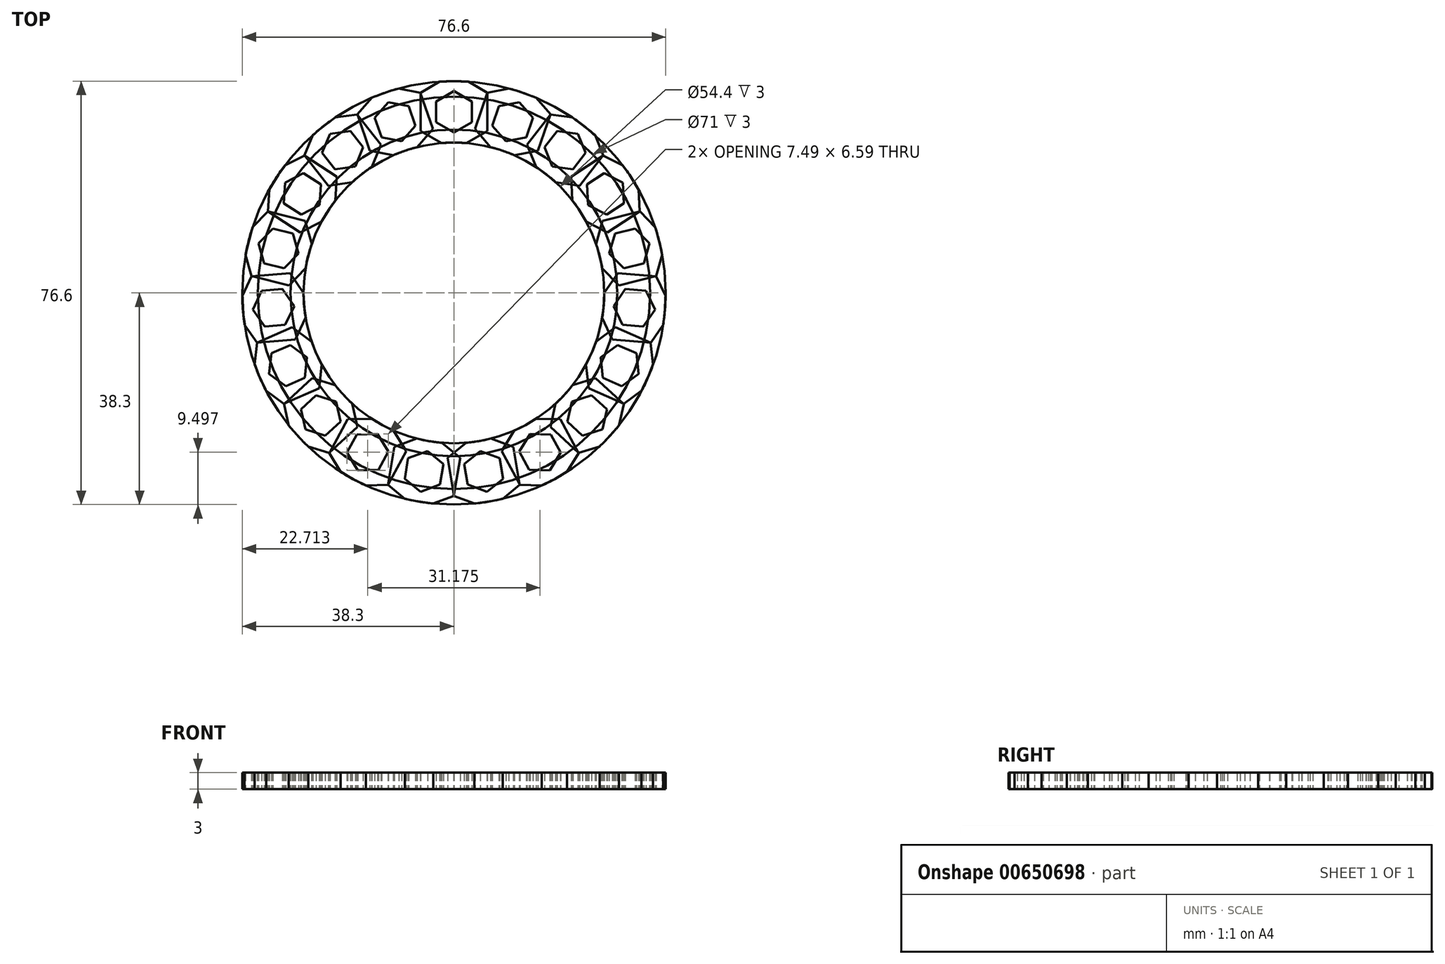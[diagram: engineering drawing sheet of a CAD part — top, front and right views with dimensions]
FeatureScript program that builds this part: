
annotation { "Feature Type Name" : "Feature", "Feature Type Description" : "" }
export const myFeature = defineFeature(function(context is Context, id is Id, definition is map)
    precondition{}
    {
        {
            var Q0;
            Q0=qCreatedBy(makeId("Top.planeOp"),FACE);
            var sketch = newSketch(context, id + "F0", { "sketchPlane" : qUnion([Q0])});
            skCircle(sketch, "E0", {"center": v(0, 0) * mm, "radius": 27.2 * mm});
            skCircle(sketch, "E1", {"center": v(0, 0) * mm, "radius": 38.3 * mm});
            skCircle(sketch, "E2", {"center": v(0, 0) * mm, "radius": 29.55 * mm});
            skCircle(sketch, "E3", {"center": v(0, 0) * mm, "radius": 35.5 * mm});
            skSolve(sketch);
        }
        {
            var Q0;
            Q0=qCreatedBy(makeId("Top.planeOp"),FACE);
            var sketch = newSketch(context, id + "F1", { "sketchPlane" : qUnion([Q0])});
            skCircle(sketch, "E4", {"center": v(0, 0) * mm, "radius": 27.2 * mm});
            skCircle(sketch, "E5", {"center": v(0, 0) * mm, "radius": 38.3 * mm});
            skLineSegment(sketch, "E6", {"start": v(0, 27.2) * mm, "end": v(0, 38.3) * mm});
            skCircle(sketch, "E7.cCircle", {"center": v(0, 32.75) * mm, "radius": 6.96 * mm, "construction": true});
            skLineSegment(sketch, "E7.0", {"start": v(0, 39.71) * mm, "end": v(6.03, 36.23) * mm});
            skLineSegment(sketch, "E7.1", {"start": v(6.03, 36.23) * mm, "end": v(6.03, 29.27) * mm});
            skLineSegment(sketch, "E7.2", {"start": v(6.03, 29.27) * mm, "end": v(0, 25.79) * mm});
            skLineSegment(sketch, "E7.3", {"start": v(0, 25.79) * mm, "end": v(-6.03, 29.27) * mm});
            skLineSegment(sketch, "E7.4", {"start": v(-6.03, 29.27) * mm, "end": v(-6.03, 36.23) * mm});
            skLineSegment(sketch, "E7.5", {"start": v(-6.03, 36.23) * mm, "end": v(0, 39.71) * mm});
            skCircle(sketch, "E8.cCircle", {"center": v(0, 32.75) * mm, "radius": 3.75 * mm, "construction": true});
            skLineSegment(sketch, "E8.0", {"start": v(0, 36.5) * mm, "end": v(3.25, 34.62) * mm});
            skLineSegment(sketch, "E8.1", {"start": v(3.25, 34.62) * mm, "end": v(3.25, 30.88) * mm});
            skLineSegment(sketch, "E8.2", {"start": v(3.25, 30.88) * mm, "end": v(0, 29) * mm});
            skLineSegment(sketch, "E8.3", {"start": v(0, 29) * mm, "end": v(-3.25, 30.88) * mm});
            skLineSegment(sketch, "E8.4", {"start": v(-3.25, 30.88) * mm, "end": v(-3.25, 34.62) * mm});
            skLineSegment(sketch, "E8.5", {"start": v(-3.25, 34.62) * mm, "end": v(0, 36.5) * mm});
            skSolve(sketch);
        }
        {
            var Q0;
            {var subQ11=sQuery(id+"F1.wireOp",EDGE,"E7.1");Q0=makeQuery(id+"F1.imprint","IMPRINT",FACE,{"disambiguationData":[TD([[makeQuery(id+"F1.imprint","IMPRINT",EDGE,{"derivedFrom":subQ11}),-1.0]])]});}
            var Q1;
            {var subQ6=sQuery(id+"F1.wireOp",EDGE,"E7.4");Q1=makeQuery(id+"F1.imprint","IMPRINT",FACE,{"disambiguationData":[TD([[makeQuery(id+"F1.imprint","IMPRINT",EDGE,{"derivedFrom":subQ6}),-1.0]])]});}
            extrude(context, id + "F2", {"entities" : qUnion([Q0, Q1]), "depth" : 3 * mm, "offsetDistance" : 25 * mm});
        }
        {
            var Q0;
            Q0=qCreatedBy(makeId("Right.planeOp"),FACE);
            var sketch = newSketch(context, id + "F3", { "sketchPlane" : qUnion([Q0])});
            skLineSegment(sketch, "E9", {"start": v(0, 42.83) * mm, "end": v(0, -44.17) * mm});
            skSolve(sketch);
        }
        {
            var Q0;
            Q0=makeQuery(id+"F2.opExtrude","SWEPT_BODY",BODY,{"disambiguationData":[OSD([sQuery(id+"F1.wireOp",EDGE,"E4"),sQuery(id+"F1.wireOp",EDGE,"E5"),sQuery(id+"F1.wireOp",EDGE,"E7.0"),sQuery(id+"F1.wireOp",EDGE,"E7.1"),sQuery(id+"F1.wireOp",EDGE,"E7.2"),sQuery(id+"F1.wireOp",EDGE,"E7.3"),sQuery(id+"F1.wireOp",EDGE,"E7.4"),sQuery(id+"F1.wireOp",EDGE,"E7.5"),sQuery(id+"F1.wireOp",EDGE,"E8.0"),sQuery(id+"F1.wireOp",EDGE,"E8.1"),sQuery(id+"F1.wireOp",EDGE,"E8.2"),sQuery(id+"F1.wireOp",EDGE,"E8.3"),sQuery(id+"F1.wireOp",EDGE,"E8.4"),sQuery(id+"F1.wireOp",EDGE,"E8.5")])]});
            var Q1;
            Q1=sQuery(id+"F3.wireOp",EDGE,"E9");
            circularPattern(context, id + "F4", {"entities" : qUnion([Q0]), "axis" : qUnion([Q1]), "angle" : 360 * degree, "instanceCount" : 19, "oppositeDirection" : true, "equalSpace" : true});
        }
        {
            var Q0;
            Q0=makeQuery(id+"F0.imprint","IMPRINT",FACE,{"disambiguationData":[TD([[makeQuery(id+"F0.imprint","IMPRINT",EDGE,{"derivedFrom":sQuery(id+"F0.wireOp",EDGE,"E1")}),1.0]])]});
            var Q1;
            Q1=makeQuery(id+"F0.imprint","IMPRINT",FACE,{"disambiguationData":[TD([[makeQuery(id+"F0.imprint","IMPRINT",EDGE,{"derivedFrom":sQuery(id+"F0.wireOp",EDGE,"E0")}),-1.0]])]});
            extrude(context, id + "F5", {"entities" : qUnion([Q0, Q1]), "depth" : 3 * mm, "offsetDistance" : 25 * mm});
        }
    });
